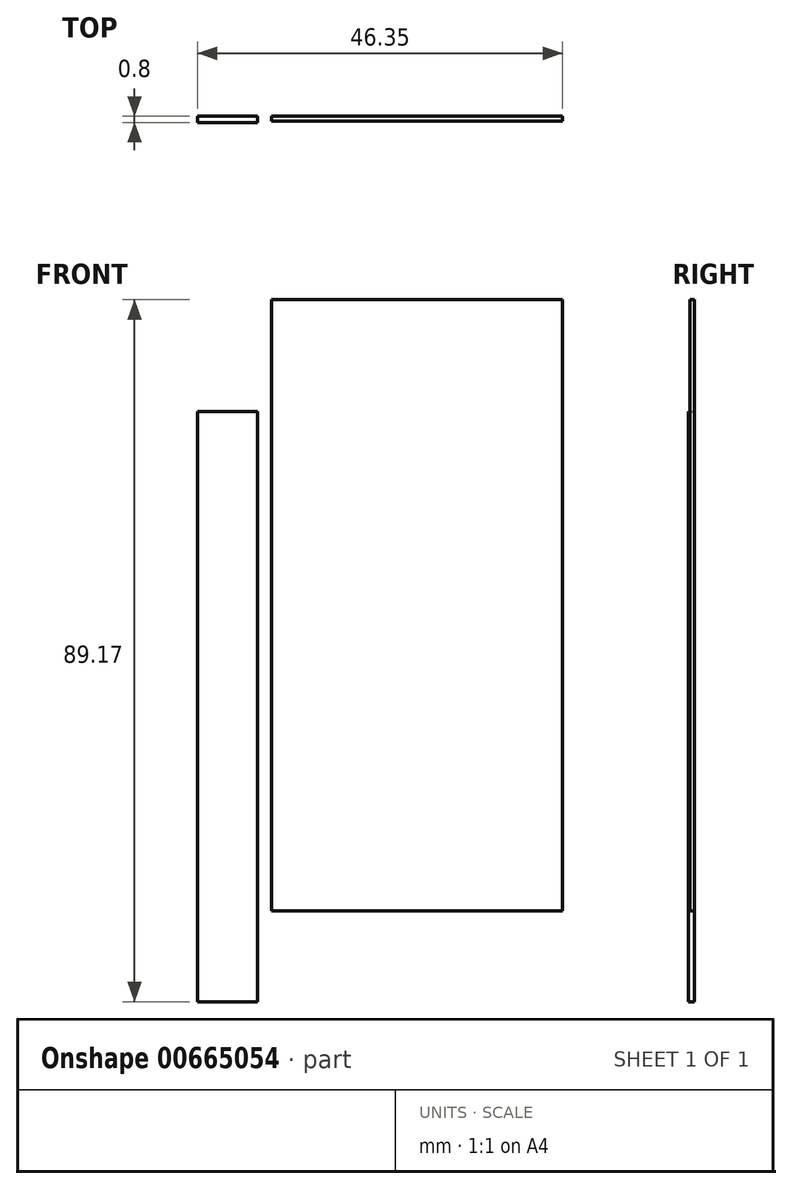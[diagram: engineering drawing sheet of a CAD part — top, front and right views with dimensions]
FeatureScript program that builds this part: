
annotation { "Feature Type Name" : "Feature", "Feature Type Description" : "" }
export const myFeature = defineFeature(function(context is Context, id is Id, definition is map)
    precondition{}
    {
        {
            var Q0;
            Q0=qCreatedBy(makeId("Front.planeOp"),FACE);
            var sketch = newSketch(context, id + "F0", { "sketchPlane" : qUnion([Q0])});
            skLineSegment(sketch, "E0.bottom", {"start": v(-9.03, -24.65) * mm, "end": v(27.89, -24.65) * mm});
            skLineSegment(sketch, "E0.top", {"start": v(-9.03, 53.01) * mm, "end": v(27.89, 53.01) * mm});
            skLineSegment(sketch, "E0.left", {"start": v(-9.03, -24.65) * mm, "end": v(-9.03, 53.01) * mm});
            skLineSegment(sketch, "E0.right", {"start": v(27.89, -24.65) * mm, "end": v(27.89, 53.01) * mm});
            skSolve(sketch);
        }
        {
            var Q0;
            Q0=makeQuery(id+"F0.imprint","IMPRINT",FACE,{"disambiguationData":[TD([[makeQuery(id+"F0.imprint","IMPRINT",EDGE,{"derivedFrom":sQuery(id+"F0.wireOp",EDGE,"E0.bottom")}),1.0]])]});
            extrude(context, id + "F1", {"entities" : qUnion([Q0]), "depth" : 0.6 * mm, "offsetDistance" : 25 * mm});
        }
        {
            var Q0;
            Q0=qCreatedBy(makeId("Front.planeOp"),FACE);
            var sketch = newSketch(context, id + "F2", { "sketchPlane" : qUnion([Q0])});
            skLineSegment(sketch, "E1.bottom", {"start": v(-18.46, -36.16) * mm, "end": v(-10.83, -36.16) * mm});
            skLineSegment(sketch, "E1.top", {"start": v(-18.46, 38.83) * mm, "end": v(-10.83, 38.83) * mm});
            skLineSegment(sketch, "E1.left", {"start": v(-18.46, -36.16) * mm, "end": v(-18.46, 38.83) * mm});
            skLineSegment(sketch, "E1.right", {"start": v(-10.83, -36.16) * mm, "end": v(-10.83, 38.83) * mm});
            skSolve(sketch);
        }
        {
            var Q0;
            Q0 = qSketchRegion(id + "F2", true);
            extrude(context, id + "F3", {"entities" : qUnion([Q0]), "depth" : 0.8 * mm, "offsetDistance" : 25 * mm});
        }
    });
